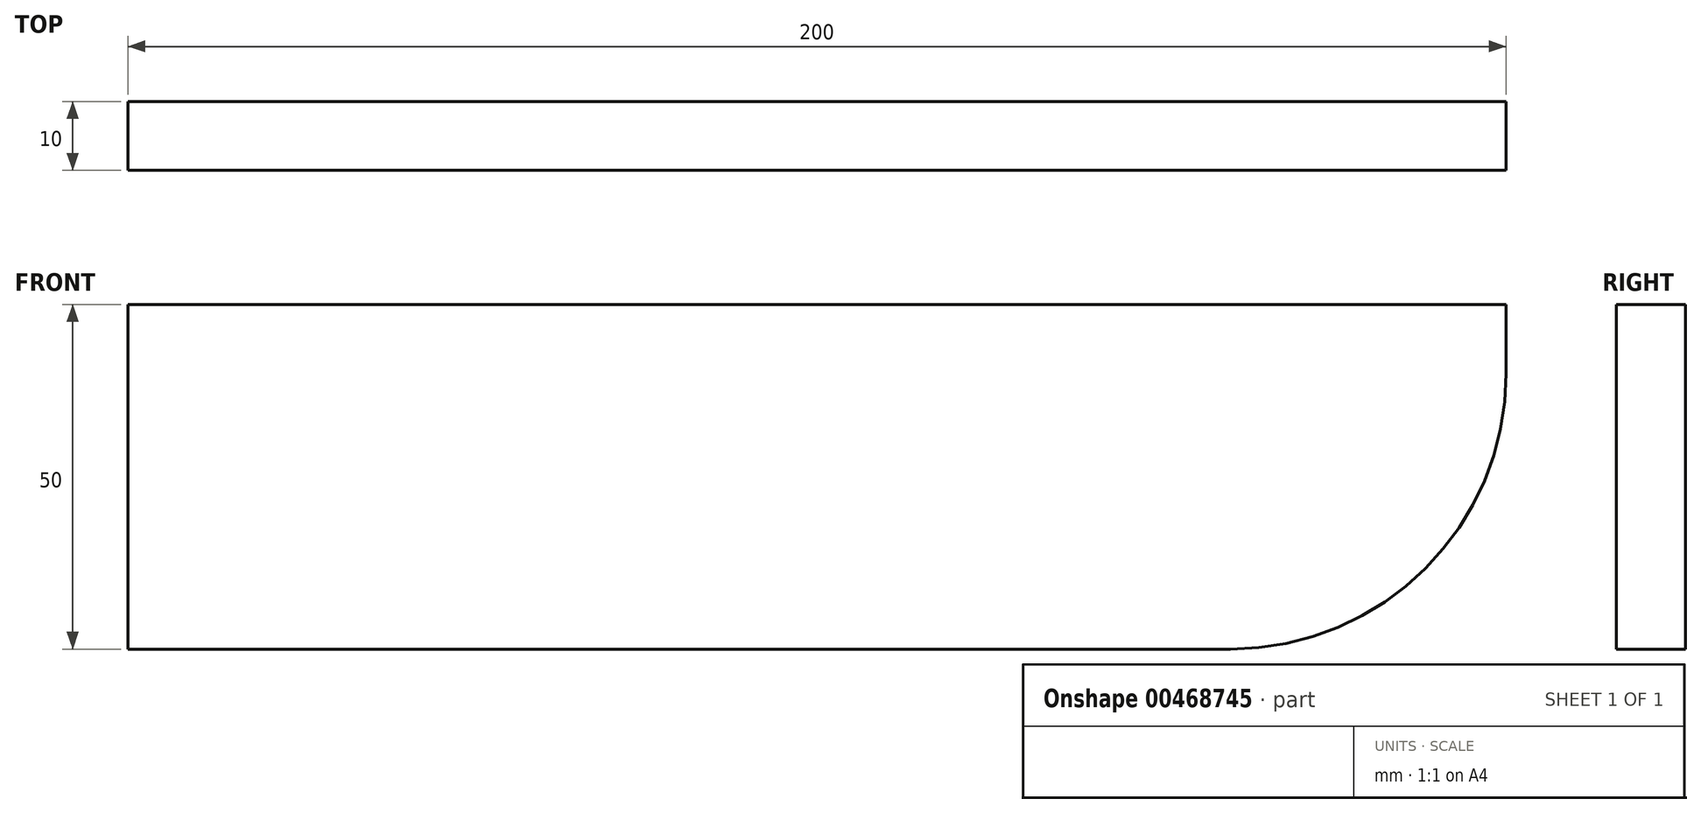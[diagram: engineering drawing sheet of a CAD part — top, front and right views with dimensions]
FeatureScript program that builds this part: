
annotation { "Feature Type Name" : "Feature", "Feature Type Description" : "" }
export const myFeature = defineFeature(function(context is Context, id is Id, definition is map)
    precondition{}
    {
        {
            var Q0;
            Q0=qCreatedBy(makeId("Front.planeOp"),FACE);
            var sketch = newSketch(context, id + "F0", { "sketchPlane" : qUnion([Q0])});
            skLineSegment(sketch, "E0.bottom", {"start": v(100, 25) * mm, "end": v(-100, 25) * mm});
            skLineSegment(sketch, "E0.top", {"start": v(60, -25) * mm, "end": v(-100, -25) * mm});
            skLineSegment(sketch, "E0.left", {"start": v(100, 25) * mm, "end": v(100, 15) * mm});
            skLineSegment(sketch, "E0.right", {"start": v(-100, 25) * mm, "end": v(-100, -25) * mm});
            skPoint(sketch, "E0.middle", {"position": v(0, 0) * mm});
            skPoint(sketch, "E1.visualSharp", {"position": v(100, -25) * mm});
            skArc(sketch, "E1.filletArc", {"start": v(60, -25) * mm, "mid": v(88.28, -13.28) * mm, "end": v(100, 15) * mm});
            skSolve(sketch);
        }
        {
            var Q0;
            Q0=makeQuery(id+"F0.imprint","IMPRINT",FACE,{"disambiguationData":[TD([[makeQuery(id+"F0.imprint","IMPRINT",EDGE,{"derivedFrom":sQuery(id+"F0.wireOp",EDGE,"E0.bottom")}),1.0]])]});
            extrude(context, id + "F1", {"entities" : qUnion([Q0]), "depth" : 10 * mm});
        }
    });
